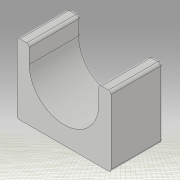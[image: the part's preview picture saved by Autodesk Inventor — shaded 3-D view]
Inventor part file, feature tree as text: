
AUTODESK INVENTOR PART (.ipt)
format: ipt  version: 2018 (Build 220112000, 112)  size: 174,592 bytes
history: native  units: in
note: dims shown in document units (in); Inventor stores cm internally (conversion verified against a paired STEP export)
features: extrude x4, sketch x4, other x2, fillet x1, reference x1
ambient origin geometry x8: Origin, YZ Plane, XZ Plane, XY Plane, X Axis, Y Axis, Z Axis, Center Point
bodies: Body1 (feature_tree)
feature tree (12):
  extrude  "Extrusion6"  Depth=0.681in
  extrude  "Extrusion7"  Depth=0.5in TaperAngle=0.0deg
  extrude  "Extrusion8"  Depth=0.003in
  fillet  "Fillet2"  Radius=0.003in
  extrude  "Extrusion9"  Depth=0.5in TaperAngle=0.0deg
  sketch  "Sketch6"  dims[d35=0.911in d36=0.681in]
  sketch  "Sketch7"  dims[d37=0.5in d38=0.0in d39=0.5in d40=0.0in]
  reference  "Reference1"
  sketch  "Sketch8"  dims[d41=0.003in d42=0.003in d43=0.003in]
  sketch  "Sketch9"  dims[d44=0.003in d45=0.5in d46=0.0in d47=0.025in d48=0.025in d49=0.0in]
  other  "Assembly1"
  other  "Jig 4:1"
